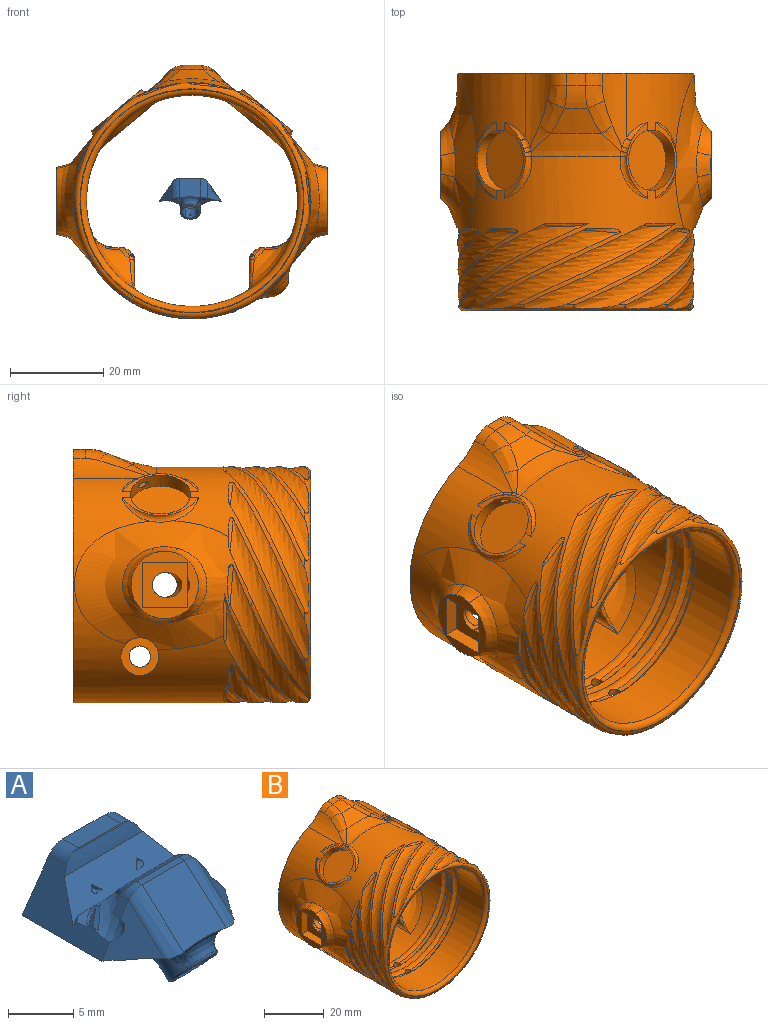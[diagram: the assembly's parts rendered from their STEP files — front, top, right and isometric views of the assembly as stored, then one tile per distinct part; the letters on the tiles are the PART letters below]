
ASSEMBLY  parts=2 mates=1
PART A: 99 faces, bbox 25.1x15.8x9.1 mm
  f0: cylinder r=22.62mm len=9.01mm, axis (0,1,0), area 27.3mm2, adj f1,f94,f95,f96,f97,f98
  f1: bspline ~7.37x6.18mm, area 15mm2, adj f0,f2,f93,f98
  f2: bspline ~5.24x2.07mm, area 1.4mm2, adj f1,f3,f90,f91,f92,f98
  f3: plane 0.6x0.26mm, normal (0,-0.74,-0.67), area 0.1mm2, adj f2,f4,f89
  f4: torus R=3.45mm, axis (0,0.74,0.67), area 0.5mm2, adj f3,f5,f85,f92
  f5: sphere r=1.27mm, area 1.7mm2, adj f4,f6,f89
  f6: bspline ~3.09x2.93mm, area 4.8mm2, adj f5,f7,f84,f85
  f7: cylinder r=22.62mm len=2.43mm, axis (0,1,0), area 1.8mm2, adj f6,f8,f89,f90,f98
  f8: extruded ~4.89x4.5mm, area 9.2mm2, adj f7,f9,f83,f84,f98
  f9: cylinder r=1.78mm len=1.46mm, axis (0,1,0), area 1.3mm2, adj f8,f10,f81,f82
  f10: plane 4.57x0.58mm, normal (0,0,1), area 2.6mm2, adj f9,f11,f80,f83
  f11: cylinder r=1.78mm len=1.46mm, axis (0,1,0), area 1.3mm2, adj f10,f12,f78,f79
  f12: extruded ~4.89x4.5mm, area 9.2mm2, adj f11,f13,f76,f77,f83
  f13: cylinder r=22.62mm len=2.43mm, axis (0,1,0), area 1.8mm2, adj f12,f14,f74,f75,f77
  f14: bspline ~3.01x1.22mm, area 1.1mm2, adj f13,f15,f74,f77
  f15: bspline ~5.24x2.07mm, area 1.4mm2, adj f14,f16,f19,f72,f73,f77
  f16: plane 0.6x0.26mm, normal (0,-0.74,-0.67), area 0.1mm2, adj f15,f17,f74
  f17: torus R=3.45mm, axis (0,0.74,0.67), area 0.5mm2, adj f16,f18,f19,f85
  f18: sphere r=1.27mm, area 1.9mm2, adj f17,f74,f75
  f19: bspline ~2.56x1.98mm, area 2.3mm2, adj f15,f17,f20,f85
  f20: bspline ~0.88x0.63mm, area 0.1mm2, adj f19,f21,f71,f72
  f21: plane 5.28x2.07mm, normal (-1,0,0), area 2.4mm2, adj f20,f22,f70,f71,f72,f95
  f22: cylinder r=1.14mm len=3.88mm, axis (0,1,0), area 5.6mm2, adj f21,f23,f70,f95
  f23: cylinder r=22.62mm len=9.01mm, axis (0,1,0), area 27.3mm2, adj f22,f24,f73,f77,f95,f96
  f24: plane 8.68x4.33mm, normal (-0.82,0,0.57), area 24.6mm2, adj f23,f25,f54,f61,f62,f67,f68,f69
  f25: bspline ~12.73x12.04mm, area 13.1mm2, adj f24,f26,f28,f39,f49,f51,f52,f53
  f26: bspline ~2.41x2.24mm, area 1.1mm2, adj f25,f27,f69
  f27: plane 2.04x1.79mm, normal (-0.49,0.45,0.75), area 1mm2, adj f26,f69
  f28: plane 10.42x1.4mm, normal (0,0.74,0.67), area 7.1mm2, adj f25,f29,f30,f31,f34,f39,f62,f67
  f29: plane 0.84x0.62mm, normal (0.49,0.45,0.75), area 0.2mm2, adj f28,f30,f62,f97
  f30: cone r=1.65mm half-angle=45deg, axis (0.49,0.45,0.75), area 1.3mm2, adj f28,f29,f31,f97
  f31: cylinder r=1.65mm len=2.41mm, axis (0.49,0.45,0.75), area 0.8mm2, adj f28,f30,f32,f33,f34,f97
  f32: plane 2.04x1.79mm, normal (0.49,0.45,0.75), area 1mm2, adj f31,f33
  f33: bspline ~2.41x2.24mm, area 1.1mm2, adj f31,f32,f34
  f34: bspline ~12.73x12.04mm, area 13.1mm2, adj f28,f31,f33,f35,f37,f38,f39,f49
  f35: cone r=1.65mm half-angle=45deg, axis (0.49,0.45,0.75), area 1.2mm2, adj f34,f36,f38,f49,f82
  f36: plane 0.64x0.6mm, normal (0.49,0.45,0.75), area 0mm2, adj f35,f49,f81,f82
  f37: bspline ~1.57x1.5mm, area 0mm2, adj f34,f38
  f38: cylinder r=1.65mm len=2.12mm, axis (0.49,0.45,0.75), area 1.1mm2, adj f34,f35,f37,f82
  f39: cylinder r=1.68mm len=8.2mm, axis (0,-0.74,-0.67), area 62.2mm2, adj f25,f28,f34,f40,f46,f49
  f40: plane 3.86x2.87mm, normal (0,-0.74,-0.67), area 2.9mm2, adj f39,f41,f42,f44,f45,f46
  f41: bspline ~0.65x0.63mm, area 0.1mm2, adj f40,f42,f45,f76
  f42: bspline ~2.91x0.73mm, area 1mm2, adj f40,f41,f43,f44
  f43: bspline ~4.87x2.01mm, area 6mm2, adj f42,f76,f83,f84
  f44: bspline ~0.68x0.65mm, area 0.1mm2, adj f40,f42,f45,f84
  f45: torus R=1.93mm, axis (0,-0.74,-0.67), area 3.9mm2, adj f40,f41,f44,f85
  f46: extruded ~4.61x4.6mm, area 22.2mm2, adj f39,f40,f47,f48
  f47: plane 0.47x0.42mm, normal (0,-0.65,0.76), area 0.2mm2, adj f46,f48
  f48: plane 0.55x0.13mm, normal (0,0.37,-0.93), area 0mm2, adj f46,f47
  f49: plane 6.3x1.74mm, normal (0,0.74,0.67), area 7.8mm2, adj f25,f34,f35,f36,f39,f50,f51,f79
  f50: plane 0.64x0.6mm, normal (-0.49,0.45,0.75), area 0mm2, adj f49,f51,f78,f79
  f51: cone r=2.16mm half-angle=45deg, axis (-0.49,0.45,0.75), area 1.2mm2, adj f25,f49,f50,f53,f78
  f52: bspline ~1.57x1.5mm, area 0mm2, adj f25,f53
  f53: cylinder r=1.65mm len=2.12mm, axis (-0.49,0.45,0.75), area 1.1mm2, adj f25,f51,f52,f78
  f54: cylinder r=1.78mm len=1.89mm, axis (0,1,0), area 2.9mm2, adj f24,f55,f60,f61,f96
  f55: plane 4.57x1.68mm, normal (0,0,1), area 7.7mm2, adj f54,f56,f59,f96
  f56: cylinder r=1.78mm len=1.89mm, axis (0,1,0), area 2.9mm2, adj f55,f57,f61,f96,f97
  f57: bspline ~2.18x1.54mm, area 0mm2, adj f56,f58,f59
  f58: plane 5.9x0.15mm, normal (0,-0.09,-1), area 0.5mm2, adj f57,f59,f60,f61
  f59: plane 4.57x0.11mm, normal (0,-0.91,0.41), area 0.6mm2, adj f55,f57,f58,f60
  f60: bspline ~0.64x0.22mm, area 0mm2, adj f54,f58,f59
  f61: extruded ~8.51x1.37mm, area 10.7mm2, adj f24,f54,f56,f58,f62,f97
  f62: plane 11.86x2.65mm, normal (0,-0.67,0.74), area 30.4mm2, adj f24,f28,f29,f61,f63,f64,f65,f66
  f63: plane 0.8x0.76mm, normal (-0.7,-0.71,-0.05), area 0.2mm2, adj f62,f64
  f64: bspline ~1.01x0.98mm, area 0.4mm2, adj f62,f63
  f65: plane 0.8x0.76mm, normal (0.7,-0.71,-0.05), area 0.2mm2, adj f62,f66
  f66: bspline ~1.01x0.98mm, area 0.4mm2, adj f62,f65
  f67: plane 0.84x0.62mm, normal (-0.49,0.45,0.75), area 0.2mm2, adj f24,f28,f62,f68
  f68: cone r=2.16mm half-angle=45deg, axis (-0.49,0.45,0.75), area 1.3mm2, adj f24,f28,f67,f69
  f69: cylinder r=1.65mm len=2.41mm, axis (-0.49,0.45,0.75), area 0.8mm2, adj f24,f25,f26,f27,f28,f68
  f70: bspline ~5.41x3.02mm, area 6.3mm2, adj f21,f22,f72,f73
  f71: cylinder r=1.14mm len=2.77mm, axis (0,0.74,0.67), area 1.7mm2, adj f20,f21,f85,f95
  f72: bspline ~0.93x0.84mm, area 0.1mm2, adj f15,f20,f21,f70
  f73: bspline ~7.32x6.17mm, area 15mm2, adj f15,f23,f70,f77
  f74: bspline ~1.04x0.84mm, area 0.7mm2, adj f13,f14,f16,f18
  f75: bspline ~3.21x3.17mm, area 4.8mm2, adj f13,f18,f76,f85
  f76: bspline ~2.38x2.3mm, area 0.8mm2, adj f12,f41,f43,f75,f85
  f77: plane 4.35x4.03mm, normal (-0.73,-0.46,0.51), area 10.2mm2, adj f12,f13,f14,f15,f23,f24,f25,f73
  f78: plane 1.34x1.03mm, normal (-0.82,0,0.57), area 1.3mm2, adj f11,f25,f50,f51,f53,f77
  f79: bspline ~1.46x0.96mm, area 1mm2, adj f11,f49,f50,f80
  f80: plane 4.57x0.57mm, normal (0,0.41,0.91), area 2.8mm2, adj f10,f49,f79,f81
  f81: bspline ~1.46x0.96mm, area 1mm2, adj f9,f36,f49,f80
  f82: plane 1.34x1.03mm, normal (0.82,0,0.57), area 1.3mm2, adj f9,f34,f35,f36,f38,f98
  f83: plane 4.71x4.64mm, normal (0,-0.67,0.74), area 27.2mm2, adj f8,f10,f12,f43
  f84: bspline ~2.21x2.14mm, area 0.8mm2, adj f6,f8,f43,f44,f85
  f85: cylinder r=2.18mm len=4.83mm, axis (0,0.74,0.67), area 15.5mm2, adj f4,f6,f17,f19,f45,f71,f75,f76
  f86: cylinder r=1.14mm len=2.77mm, axis (0,0.74,0.67), area 1.7mm2, adj f85,f87,f88,f95
  f87: plane 5.28x2.07mm, normal (1,0,0), area 2.4mm2, adj f86,f88,f91,f93,f94,f95
  f88: bspline ~0.93x0.6mm, area 0.1mm2, adj f86,f87,f91,f92
  f89: bspline ~1.04x0.84mm, area 0.7mm2, adj f3,f5,f7,f90
  f90: bspline ~3.01x1.22mm, area 1.1mm2, adj f2,f7,f89,f98
  f91: bspline ~0.96x0.88mm, area 0.1mm2, adj f2,f87,f88,f93
  f92: bspline ~2.56x1.98mm, area 2.3mm2, adj f2,f4,f85,f88
  f93: bspline ~5.41x3.02mm, area 6.3mm2, adj f1,f87,f91,f94
  f94: cylinder r=1.14mm len=3.88mm, axis (0,1,0), area 5.6mm2, adj f0,f87,f93,f95
  f95: plane 10.79x5.27mm, normal (0,0.37,-0.93), area 27mm2, adj f0,f21,f22,f23,f71,f85,f86,f87
  f96: plane 13.37x4.96mm, normal (0,1,0), area 39.8mm2, adj f0,f23,f24,f54,f55,f56,f97
  f97: plane 8.68x4.33mm, normal (0.82,0,0.57), area 24.6mm2, adj f0,f29,f30,f31,f34,f56,f61,f62
  f98: plane 4.35x4.03mm, normal (0.73,-0.46,0.51), area 10.2mm2, adj f0,f1,f2,f7,f8,f34,f82,f90
PART B: 277 faces, bbox 65.1x60.6x65.1 mm
  f0: cylinder r=7.23mm len=4mm, axis (-1,0,0), area 0mm2, adj f1,f276
  f1: plane 14.98x14.98mm, normal (-1,0,0), area 70mm2, adj f0,f2,f269,f270,f271,f272,f273,f274
  f2: cylinder r=7.23mm len=4mm, axis (-1,0,0), area 0mm2, adj f1,f3
  f3: bspline ~8.56x3.63mm, area 14.9mm2, adj f2,f4,f269,f270
  f4: bspline ~38.72x27.55mm, area 617.9mm2, adj f3,f5,f258,f259,f260,f261,f262,f263
  f5: cylinder r=4.06mm len=11.07mm, axis (-1,0,0), area 179.5mm2, adj f4,f6,f243,f244,f245,f246,f247,f248
  f6: bspline ~3.39x1.85mm, area 1.2mm2, adj f5,f7,f243,f257
  f7: cylinder r=1.4mm len=10.89mm, axis (0,1,0), area 9.7mm2, adj f6,f8,f33,f241,f242
  f8: plane 4.01x3.6mm, normal (1,0,0), area 4.9mm2, adj f7,f9,f243
  f9: bspline ~6.62x4.96mm, area 8.1mm2, adj f8,f10,f241,f242,f244
  f10: torus R=4.32mm, axis (1,0,0), area 1.1mm2, adj f9,f11,f32,f245
  f11: cylinder r=5.33mm len=8.95mm, axis (-1,0,0), area 9mm2, adj f10,f12,f19,f26,f31,f241
  f12: bspline ~6.6x5.33mm, area 15.1mm2, adj f11,f13,f31,f241
  f13: cylinder r=6.1mm len=12.19mm, axis (1,0,0), area 17.8mm2, adj f12,f14,f33
  f14: plane 18.15x18.15mm, normal (1,0,0), area 87.2mm2, adj f13,f15,f18
  f15: cylinder r=2.67mm len=5.33mm, axis (1,0,0), area 25.9mm2, adj f14,f16,f17,f18
  f16: plane 9.65x9.65mm, normal (-1,0,0), area 66mm2, adj f15,f17,f271,f272,f274,f275
  f17: cylinder r=2.63mm len=5.26mm, axis (-0.88,-0.48,0), area 14.3mm2, adj f15,f16
  f18: cylinder r=2.63mm len=5.26mm, axis (-0.88,-0.48,0), area 0mm2, adj f14,f15
  f19: bspline ~7.89x2.23mm, area 9mm2, adj f11,f20,f22,f23,f25,f32
  f20: bspline ~0.95x0.93mm, area 0.5mm2, adj f19,f21,f22,f251
  f21: cylinder r=1.27mm len=0.41mm, axis (0,-1,0), area 0mm2, adj f20,f25,f250
  f22: bspline ~1.34x1.3mm, area 0.4mm2, adj f19,f20,f26,f252
  f23: bspline ~1.21x1.2mm, area 0.5mm2, adj f19,f24,f32,f247
  f24: cylinder r=1.27mm len=0.41mm, axis (0,-1,0), area 0mm2, adj f23,f25,f248
  f25: plane 5.51x1.07mm, normal (0.71,0,0.71), area 1.6mm2, adj f19,f21,f24,f249
  f26: torus R=4.32mm, axis (1,0,0), area 1.1mm2, adj f11,f22,f27,f253
  f27: bspline ~5.73x3.96mm, area 8.3mm2, adj f26,f28,f30,f31,f254
  f28: bspline ~4.78x1.91mm, area 2.3mm2, adj f27,f29,f31
  f29: cylinder r=1.4mm len=10.89mm, axis (0,1,0), area 10.4mm2, adj f28,f30,f33,f256
  f30: plane 4x3.6mm, normal (1,0,0), area 4.9mm2, adj f27,f29,f255
  f31: bspline ~15.45x15.15mm, area 101.4mm2, adj f11,f12,f27,f28,f33
  f32: bspline ~1.38x1.27mm, area 0.3mm2, adj f10,f19,f23,f246
  f33: cylinder r=22.62mm len=45.24mm, axis (0,1,0), area 2155mm2, adj f7,f13,f29,f31,f34,f36,f38,f213
  f34: bspline ~21x13.67mm, area 169.3mm2, adj f33,f35
  f35: plane 16.09x12.82mm, normal (-0.64,0,-0.77), area 153.3mm2, adj f34
  f36: bspline ~21x13.67mm, area 169.3mm2, adj f33,f37
  f37: plane 16.29x13.03mm, normal (0.64,0,-0.77), area 153.3mm2, adj f36
  f38: cylinder r=1.4mm len=10.89mm, axis (0,1,0), area 9.7mm2, adj f33,f39,f211,f212,f217
  f39: plane 4x3.6mm, normal (-1,0,0), area 4.9mm2, adj f38,f40,f210
  f40: torus R=4.45mm, axis (1,0,0), area 2.4mm2, adj f39,f41,f209,f211
  f41: cylinder r=4.06mm len=8.13mm, axis (-1,0,0), area 132.2mm2, adj f40,f42,f58,f198,f199,f200,f201,f202
  f42: bspline ~5.16x1.41mm, area 4.7mm2, adj f41,f43,f198,f208
  f43: plane 5.51x1.07mm, normal (-0.71,0,0.71), area 1.6mm2, adj f42,f44,f56,f57
  f44: bspline ~7.89x2.23mm, area 9mm2, adj f43,f45,f46,f51,f54,f55
  f45: bspline ~0.95x0.93mm, area 0.5mm2, adj f44,f46,f57,f199
  f46: bspline ~1.06x1.03mm, area 0.4mm2, adj f44,f45,f47,f200
  f47: torus R=4.32mm, axis (1,0,0), area 1.1mm2, adj f46,f48,f51,f201
  f48: bspline ~6.62x4.96mm, area 8.1mm2, adj f47,f49,f50,f202,f215
  f49: bspline ~4.98x2.05mm, area 2.3mm2, adj f48,f214,f215
  f50: plane 4.01x3.6mm, normal (-1,0,0), area 4.9mm2, adj f48,f203,f214
  f51: cylinder r=5.33mm len=8.94mm, axis (-1,0,0), area 9mm2, adj f44,f47,f52,f53,f215,f217
  f52: bspline ~6.63x5.64mm, area 15.1mm2, adj f51,f215,f216,f217
  f53: torus R=4.32mm, axis (1,0,0), area 1.1mm2, adj f51,f54,f205,f210
  f54: bspline ~1.34x1.3mm, area 0.4mm2, adj f44,f53,f55,f206
  f55: bspline ~1.21x1.2mm, area 0.5mm2, adj f44,f54,f56,f207
  f56: cylinder r=1.27mm len=0.41mm, axis (0,-1,0), area 0mm2, adj f43,f55,f208
  f57: cylinder r=1.27mm len=0.41mm, axis (0,-1,0), area 0mm2, adj f43,f45,f198
  f58: plane 8.13x8.13mm, normal (-1,0,0), area 35.5mm2, adj f41,f59
  f59: cylinder r=2.29mm len=4.57mm, axis (-1,0,0), area 44.4mm2, adj f58,f60,f63,f64,f65,f66
  f60: bspline ~8.22x8.05mm, area 33.7mm2, adj f59,f61,f63,f66,f258
  f61: bspline ~6.51x3.43mm, area 10.6mm2, adj f60,f62,f64,f258
  f62: cylinder r=5.33mm len=2.68mm, axis (-1,0,0), area 0mm2, adj f61,f63
  f63: torus R=0.76mm, axis (1,0,0), area 34.6mm2, adj f59,f60,f62,f64
  f64: bspline ~8.05x7.79mm, area 33.4mm2, adj f59,f61,f63,f65,f66,f258
  f65: cylinder r=4.57mm len=0.21mm, axis (0,1,0), area 0mm2, adj f59,f64,f66
  f66: bspline ~38.66x27.57mm, area 651.6mm2, adj f59,f60,f64,f65,f67,f81,f82,f84
  f67: bspline ~15.67x7.05mm, area 56.5mm2, adj f66,f68,f81,f197
  f68: plane 14.98x14.98mm, normal (1,0,0), area 70mm2, adj f67,f69,f70,f71,f72,f78,f79,f80
  f69: cylinder r=7.23mm len=4mm, axis (1,0,0), area 0mm2, adj f68,f81
  f70: cylinder r=7.23mm len=4mm, axis (1,0,0), area 0mm2, adj f68,f197
  f71: cylinder r=2.63mm len=3mm, axis (0.88,-0.48,0), area 0mm2, adj f68,f80
  f72: plane 9.65x3.05mm, normal (0,0,1), area 29.4mm2, adj f68,f73,f78,f80
  f73: plane 9.65x9.65mm, normal (1,0,0), area 66mm2, adj f72,f74,f75,f78,f79,f80
  f74: cylinder r=2.63mm len=5.26mm, axis (0.88,-0.48,0), area 14.3mm2, adj f73,f75
  f75: cylinder r=2.67mm len=5.33mm, axis (1,0,0), area 25.9mm2, adj f73,f74,f76,f77
  f76: plane 18.15x18.15mm, normal (-1,0,0), area 87.2mm2, adj f75,f77,f216
  f77: cylinder r=2.63mm len=5.26mm, axis (0.88,-0.48,0), area 0mm2, adj f75,f76
  f78: plane 9.65x3.05mm, normal (0,-1,0), area 29.4mm2, adj f68,f72,f73,f79
  f79: plane 9.65x3.05mm, normal (0,0,-1), area 29.4mm2, adj f68,f73,f78,f80
  f80: plane 11.35x4.75mm, normal (0,1,0), area 27.4mm2, adj f68,f71,f72,f73,f79
  f81: bspline ~9.08x3.85mm, area 14.9mm2, adj f66,f67,f69,f196
  f82: bspline ~3.32x2.19mm, area 0.7mm2, adj f66,f83,f84
  f83: torus R=24.4mm, axis (0,-1,0), area 5.7mm2, adj f82,f84,f258
  f84: bspline ~45.41x20.32mm, area 167.7mm2, adj f66,f82,f83,f85,f114,f258
  f85: torus R=24.02mm, axis (0,1,0), area 205mm2, adj f84,f86,f88,f89,f100,f102,f104,f106
  f86: bspline ~45.84x20.32mm, area 164.1mm2, adj f85,f87,f260
  f87: torus R=24.4mm, axis (0,-1,0), area 6.5mm2, adj f86,f260
  f88: torus R=24.02mm, axis (0,1,0), area 0mm2, adj f85,f116,f117
  f89: plane 48.03x48.03mm, normal (0,-1,0), area 19.1mm2, adj f85,f90
  f90: torus R=23.89mm, axis (0,1,0), area 289.3mm2, adj f89,f91
  f91: cylinder r=22.62mm len=45.24mm, axis (0,1,0), area 1562.7mm2, adj f90,f92
  f92: torus R=22.11mm, axis (0,1,0), area 243.7mm2, adj f91,f93,f99
  f93: cylinder r=1.27mm len=2.54mm, axis (0,0,1), area 10.9mm2, adj f92,f94,f99,f104
  f94: torus R=22.11mm, axis (0,1,0), area 243.7mm2, adj f93,f95,f99
  f95: cylinder r=22.62mm len=45.24mm, axis (0,1,0), area 273.8mm2, adj f94,f96
  f96: torus R=22.11mm, axis (0,1,0), area 243.7mm2, adj f95,f97,f98
  f97: cylinder r=1.27mm len=2.54mm, axis (0,0,1), area 13.2mm2, adj f96,f98,f223,f258
  f98: cylinder r=23.79mm len=47.57mm, axis (0,1,0), area 174.3mm2, adj f96,f97,f223
  f99: cylinder r=23.79mm len=47.57mm, axis (0,1,0), area 174.3mm2, adj f92,f93,f94
  f100: bspline ~43.97x21.94mm, area 164.1mm2, adj f85,f101,f258
  f101: torus R=24.4mm, axis (0,-1,0), area 6.5mm2, adj f100,f258
  f102: bspline ~35.51x33.27mm, area 147.4mm2, adj f85,f103,f258
  f103: bspline ~9.96x3.03mm, area 0mm2, adj f102,f258
  f104: bspline ~42.71x24.3mm, area 166.1mm2, adj f85,f93,f105,f258
  f105: torus R=24.4mm, axis (0,-1,0), area 6.5mm2, adj f104,f258
  f106: bspline ~45.84x20.32mm, area 147.4mm2, adj f85,f107,f258
  f107: bspline ~8.25x7.24mm, area 0mm2, adj f106,f258
  f108: bspline ~43.97x21.94mm, area 147.4mm2, adj f85,f109,f260
  f109: bspline ~8.59x6.83mm, area 0mm2, adj f108,f260
  f110: bspline ~35.51x33.27mm, area 164.1mm2, adj f85,f111,f260
  f111: torus R=24.4mm, axis (0,-1,0), area 6.5mm2, adj f110,f260
  f112: bspline ~42.71x24.3mm, area 147.4mm2, adj f85,f113,f260
  f113: bspline ~9.82x3.52mm, area 0mm2, adj f112,f260
  f114: cylinder r=25.29mm len=20.1mm, axis (0,1,0), area 23.9mm2, adj f66,f84,f85,f116
  f115: bspline ~12.27x1.61mm, area 0mm2, adj f66,f116
  f116: bspline ~38.75x29.76mm, area 155.4mm2, adj f66,f85,f88,f114,f115,f117
  f117: cylinder r=25.29mm len=25.96mm, axis (0,1,0), area 30.1mm2, adj f66,f85,f88,f116,f118
  f118: bspline ~40.31x27.89mm, area 154.5mm2, adj f66,f85,f117,f119,f260
  f119: bspline ~10.14x5.35mm, area 3.5mm2, adj f66,f118,f260
  f120: bspline ~16.5x7.09mm, area 20.2mm2, adj f66,f121,f122,f258,f260
  f121: cylinder r=6.99mm len=1.71mm, axis (0.64,0,0.77), area 0mm2, adj f120,f122
  f122: plane 16.87x5.02mm, normal (0.64,0,0.77), area 15.2mm2, adj f120,f121,f123,f258,f260
  f123: cylinder r=6.48mm len=12.95mm, axis (0.64,0,0.77), area 121.4mm2, adj f122,f124,f193,f194,f195,f258,f260
  f124: bspline ~9.24x8.08mm, area 55.1mm2, adj f123,f125,f127,f128,f192,f193,f226,f227
  f125: plane 0.91x0.6mm, normal (0.73,-0.46,0.51), area 0.3mm2, adj f124,f126,f127,f227
  f126: plane 0.91x0.89mm, normal (0.23,-0.65,0.72), area 0.3mm2, adj f125,f127,f226,f227
  f127: plane 0.87x0.79mm, normal (0.16,-0.99,0.04), area 0.2mm2, adj f124,f125,f126,f226
  f128: plane 2.07x1.92mm, normal (0.16,-0.99,0.04), area 0.7mm2, adj f124,f129,f191,f192,f226
  f129: extruded ~0.4x0.32mm, area 0mm2, adj f128,f130,f191,f192
  f130: cylinder r=2.03mm len=8.49mm, axis (0,1,0), area 14.4mm2, adj f129,f131,f174,f175,f176,f177,f178,f191
  f131: plane 4.57x1.49mm, normal (0,0,-1), area 6.8mm2, adj f130,f132,f174,f191
  f132: cylinder r=2.03mm len=8.49mm, axis (0,1,0), area 14.4mm2, adj f131,f133,f171,f172,f174,f176,f177,f178
  f133: extruded ~0.4x0.32mm, area 0mm2, adj f132,f134,f171,f191
  f134: plane 2.07x1.92mm, normal (-0.16,-0.99,0.04), area 0.7mm2, adj f133,f135,f171,f191,f221
  f135: bspline ~9.24x8.08mm, area 55.1mm2, adj f134,f136,f137,f168,f170,f171,f220,f221
  f136: extruded ~1.73x1.69mm, area 0mm2, adj f135,f137
  f137: cylinder r=6.48mm len=12.95mm, axis (-0.64,0,0.77), area 121.4mm2, adj f135,f136,f138,f139,f166,f258,f260
  f138: plane 12.95x9.92mm, normal (-0.64,0,0.77), area 131.8mm2, adj f137
  f139: plane 16.86x5.01mm, normal (-0.64,0,0.77), area 15.2mm2, adj f137,f140,f141,f162,f163,f164,f165,f258
  f140: bspline ~6.73x5.44mm, area 4.2mm2, adj f139,f141,f258
  f141: bspline ~3.06x2.72mm, area 2.8mm2, adj f139,f140,f142,f162
  f142: cylinder r=13.97mm len=15.7mm, axis (0,1,0), area 73.4mm2, adj f141,f143,f159,f160,f161,f178,f258
  f143: bspline ~9.16x7.24mm, area 10.7mm2, adj f142,f144,f159,f162
  f144: torus R=39.26mm, axis (0,1,0), area 81.5mm2, adj f143,f145,f157,f158,f163,f260
  f145: bspline ~3.01x1.74mm, area 1.5mm2, adj f144,f146,f155,f156,f194
  f146: bspline ~2.41x1.95mm, area 1.5mm2, adj f145,f147,f157,f194
  f147: bspline ~3.43x2.83mm, area 2.8mm2, adj f146,f148,f149,f194
  f148: bspline ~6.73x5.44mm, area 4.2mm2, adj f147,f194,f258
  f149: cylinder r=13.97mm len=15.7mm, axis (0,1,0), area 73.4mm2, adj f147,f150,f153,f154,f157,f178,f258
  f150: cylinder r=5.08mm len=3.7mm, axis (0,-1,0), area 11mm2, adj f149,f151,f153,f178
  f151: cylinder r=29.1mm len=3.89mm, axis (0,1,0), area 9.9mm2, adj f150,f152,f161,f178
  f152: torus R=15.13mm, axis (0,-1,0), area 22.5mm2, adj f151,f153,f158,f160
  f153: bspline ~9.36x4.49mm, area 18.1mm2, adj f149,f150,f152,f154
  f154: bspline ~9.04x6.04mm, area 23.3mm2, adj f149,f153,f157,f158
  f155: bspline ~10.87x7.86mm, area 11.3mm2, adj f145,f156,f194,f260
  f156: cylinder r=6.99mm len=1.69mm, axis (0.64,0,0.77), area 0mm2, adj f145,f155,f194
  f157: bspline ~9.16x7.24mm, area 10.7mm2, adj f144,f146,f149,f154
  f158: cone r=29.1mm half-angle=20.6deg, axis (0,1,0), area 46.8mm2, adj f144,f152,f154,f159
  f159: bspline ~10.91x6.7mm, area 23.4mm2, adj f142,f143,f158,f160
  f160: bspline ~9.36x4.49mm, area 18.1mm2, adj f142,f152,f159,f161
  f161: cylinder r=5.08mm len=3.7mm, axis (0,1,0), area 11mm2, adj f142,f151,f160,f178
  f162: bspline ~3.13x2.12mm, area 1.5mm2, adj f139,f141,f143,f163
  f163: bspline ~4.25x2.19mm, area 1.5mm2, adj f139,f144,f162,f164,f165
  f164: cylinder r=6.99mm len=1.69mm, axis (-0.64,0,0.77), area 0mm2, adj f139,f163,f165
  f165: bspline ~10.87x7.86mm, area 11.3mm2, adj f139,f163,f164,f260
  f166: plane 16.87x5.02mm, normal (-0.64,0,0.77), area 15.2mm2, adj f137,f167,f258,f259,f260
  f167: cylinder r=6.99mm len=1.71mm, axis (-0.64,0,0.77), area 0mm2, adj f166,f259
  f168: plane 0.91x0.6mm, normal (-0.73,-0.46,0.51), area 0.3mm2, adj f135,f169,f170,f220
  f169: plane 0.91x0.89mm, normal (-0.23,-0.65,0.72), area 0.3mm2, adj f168,f170,f220,f221
  f170: plane 0.87x0.79mm, normal (-0.16,-0.99,0.04), area 0.2mm2, adj f135,f168,f169,f221
  f171: plane 1.79x1.36mm, normal (-0.73,-0.46,0.51), area 0.2mm2, adj f132,f133,f134,f135,f220
  f172: plane 2.76x0.85mm, normal (1,0,0), area 1.5mm2, adj f132,f173,f174,f176
  f173: cylinder r=1.27mm len=5.84mm, axis (-1,0,0), area 11.7mm2, adj f172,f174,f175,f176
  f174: plane 5.9x0.63mm, normal (0,0.67,-0.74), area 3.7mm2, adj f130,f131,f132,f172,f173,f175
  f175: plane 2.76x0.85mm, normal (-1,0,0), area 1.5mm2, adj f130,f173,f174,f176
  f176: plane 5.89x0.48mm, normal (0,-0.74,-0.67), area 2.6mm2, adj f130,f132,f172,f173,f175,f177
  f177: plane 4.57x4.45mm, normal (0,0,-1), area 20.3mm2, adj f130,f132,f176,f178
  f178: plane 54.36x50.57mm, normal (0,1,0), area 281.5mm2, adj f130,f132,f142,f149,f150,f151,f161,f177
  f179: bspline ~3.15x2.37mm, area 1.3mm2, adj f178,f180,f238,f239
  f180: bspline ~13.02x11.85mm, area 11.1mm2, adj f178,f179,f181,f185
  f181: bspline ~35.77x17.91mm, area 139.4mm2, adj f180,f182,f184,f218,f239
  f182: bspline ~3.64x1.93mm, area 2.1mm2, adj f181,f183,f218,f241
  f183: bspline ~4.63x2.79mm, area 4.6mm2, adj f182,f184,f240,f241
  f184: bspline ~4.26x3.17mm, area 7mm2, adj f181,f183,f240
  f185: bspline ~2.23x0.82mm, area 0.6mm2, adj f178,f180,f218,f219
  f186: bspline ~3.31x2.12mm, area 1.3mm2, adj f178,f187,f228,f229
  f187: bspline ~13.94x10.81mm, area 11.1mm2, adj f178,f186,f188,f190
  f188: bspline ~36.76x15.67mm, area 139.4mm2, adj f187,f189,f229,f233
  f189: bspline ~4.22x3.05mm, area 6.5mm2, adj f188,f230,f231,f232
  f190: bspline ~2.21x0.95mm, area 0.6mm2, adj f178,f187,f233,f234
  f191: plane 8.27x0.7mm, normal (0,-0.74,-0.67), area 0.7mm2, adj f128,f129,f130,f131,f132,f133,f134,f221
  f192: plane 1.79x1.36mm, normal (0.73,-0.46,0.51), area 0.2mm2, adj f124,f128,f129,f130,f227
  f193: extruded ~1.73x1.69mm, area 0mm2, adj f123,f124
  f194: plane 16.86x5.01mm, normal (0.64,0,0.77), area 15.2mm2, adj f123,f145,f146,f147,f148,f155,f156,f258
  f195: plane 12.95x9.92mm, normal (0.64,0,0.77), area 131.8mm2, adj f123
  f196: bspline ~15.67x7.06mm, area 56.5mm2, adj f66,f68,f81,f197
  f197: bspline ~7.96x3.72mm, area 14.9mm2, adj f66,f67,f70,f196
  f198: bspline ~1.24x1.05mm, area 0.4mm2, adj f41,f42,f57,f199
  f199: bspline ~0.71x0.7mm, area 0.3mm2, adj f41,f45,f198,f200
  f200: bspline ~0.52x0.52mm, area 0.1mm2, adj f41,f46,f199,f201
  f201: torus R=4.45mm, axis (-1,0,0), area 0.5mm2, adj f41,f47,f200,f202
  f202: bspline ~2.28x1.34mm, area 0.9mm2, adj f41,f48,f201,f203
  f203: torus R=4.45mm, axis (1,0,0), area 2.4mm2, adj f41,f50,f202,f204
  f204: bspline ~3.39x1.85mm, area 1.2mm2, adj f41,f203,f213,f214
  f205: torus R=4.45mm, axis (-1,0,0), area 0.5mm2, adj f41,f53,f206,f209
  f206: bspline ~0.48x0.48mm, area 0.1mm2, adj f41,f54,f205,f207
  f207: bspline ~0.91x0.89mm, area 0.3mm2, adj f41,f55,f206,f208
  f208: bspline ~1.24x1.05mm, area 0.4mm2, adj f41,f42,f56,f207
  f209: bspline ~2.28x1.34mm, area 0.9mm2, adj f40,f41,f205,f210
  f210: bspline ~5.73x3.96mm, area 8.3mm2, adj f39,f53,f209,f212,f217
  f211: bspline ~3.39x1.85mm, area 1.2mm2, adj f38,f40,f41,f213
  f212: bspline ~5.05x2.13mm, area 2.3mm2, adj f38,f210,f217
  f213: bspline ~2.74x0.55mm, area 0.4mm2, adj f33,f41,f204,f211
  f214: cylinder r=1.4mm len=10.89mm, axis (0,1,0), area 10.4mm2, adj f33,f49,f50,f204
  f215: bspline ~14.54x13.85mm, area 141.1mm2, adj f33,f48,f49,f51,f52
  f216: cylinder r=6.1mm len=12.19mm, axis (1,0,0), area 17.8mm2, adj f33,f52,f76
  f217: bspline ~13.56x13.38mm, area 101.2mm2, adj f33,f38,f51,f52,f210,f212
  f218: bspline ~29.94x15.73mm, area 33.1mm2, adj f33,f181,f182,f185
  f219: torus R=23mm, axis (0,-1,0), area 1.1mm2, adj f33,f178,f185,f220
  f220: plane 8.74x4.66mm, normal (0.82,0,-0.57), area 41.9mm2, adj f33,f132,f135,f168,f169,f171,f178,f219
  f221: plane 5.15x5.07mm, normal (0.73,0.46,-0.51), area 13.6mm2, adj f33,f134,f135,f169,f170,f191,f222
  f222: extruded ~5.25x4.83mm, area 11.6mm2, adj f33,f191,f221,f224
  f223: torus R=22.11mm, axis (0,1,0), area 243.7mm2, adj f33,f97,f98
  f224: plane 4.88x4.64mm, normal (0,0.67,-0.74), area 29.2mm2, adj f33,f191,f222,f225
  f225: extruded ~5.25x4.83mm, area 11.6mm2, adj f33,f191,f224,f226
  f226: plane 5.15x5.07mm, normal (-0.73,0.46,-0.51), area 13.6mm2, adj f33,f124,f126,f127,f128,f191,f225
  f227: plane 8.74x4.66mm, normal (-0.82,0,-0.57), area 41.9mm2, adj f33,f124,f125,f126,f130,f178,f192,f228
  f228: torus R=23mm, axis (0,-1,0), area 20mm2, adj f33,f178,f186,f227
  f229: bspline ~20.63x6.24mm, area 17.5mm2, adj f33,f186,f188,f230
  f230: bspline ~2.9x1.48mm, area 2.5mm2, adj f33,f189,f229,f231
  f231: bspline ~1.21x0.88mm, area 0.6mm2, adj f33,f189,f230,f232
  f232: bspline ~2.4x1.86mm, area 2.4mm2, adj f33,f189,f231,f233
  f233: bspline ~33.04x14.22mm, area 35.2mm2, adj f33,f188,f190,f232
  f234: torus R=23mm, axis (0,-1,0), area 2mm2, adj f33,f178,f190,f235
  f235: plane 7.66x3.82mm, normal (-0.38,0.92,0), area 22.3mm2, adj f33,f178,f234,f236,f258
  f236: plane 2.69x1.02mm, normal (0,1,0), area 2.7mm2, adj f33,f235,f237,f258
  f237: plane 3.18x2.68mm, normal (1,0,0), area 8.4mm2, adj f33,f178,f236,f238,f258
  f238: torus R=23mm, axis (0,-1,0), area 24.8mm2, adj f33,f178,f179,f237
  f239: bspline ~19.63x5.92mm, area 17.5mm2, adj f33,f179,f181,f240
  f240: bspline ~1.37x1.08mm, area 0.8mm2, adj f33,f183,f184,f239
  f241: bspline ~14.54x13.85mm, area 129.3mm2, adj f7,f9,f11,f12,f33,f182,f183,f242
  f242: bspline ~5.05x2.13mm, area 2.3mm2, adj f7,f9,f241
  f243: torus R=4.45mm, axis (1,0,0), area 2.4mm2, adj f5,f6,f8,f244
  f244: bspline ~2.56x1.35mm, area 0.9mm2, adj f5,f9,f243,f245
  f245: torus R=4.45mm, axis (-1,0,0), area 0.5mm2, adj f5,f10,f244,f246
  f246: bspline ~0.53x0.53mm, area 0.1mm2, adj f5,f32,f245,f247
  f247: bspline ~0.91x0.89mm, area 0.3mm2, adj f5,f23,f246,f248
  f248: bspline ~1.24x1.05mm, area 0.4mm2, adj f5,f24,f247,f249
  f249: bspline ~5.16x1.41mm, area 4.7mm2, adj f5,f25,f248,f250
  f250: bspline ~1.24x1.05mm, area 0.4mm2, adj f5,f21,f249,f251
  f251: bspline ~0.71x0.7mm, area 0.3mm2, adj f5,f20,f250,f252
  f252: bspline ~0.54x0.53mm, area 0.1mm2, adj f5,f22,f251,f253
  f253: torus R=4.45mm, axis (-1,0,0), area 0.5mm2, adj f5,f26,f252,f254
  f254: bspline ~2.56x1.35mm, area 0.9mm2, adj f5,f27,f253,f255
  f255: torus R=4.45mm, axis (1,0,0), area 2.4mm2, adj f5,f30,f254,f256
  f256: bspline ~3.39x1.85mm, area 1.2mm2, adj f5,f29,f255,f257
  f257: bspline ~2.74x0.55mm, area 0.4mm2, adj f5,f6,f33,f256
  f258: cylinder r=25.29mm len=50.57mm, axis (0,1,0), area 2231mm2, adj f4,f5,f60,f61,f64,f66,f83,f84
  f259: bspline ~16.5x7.09mm, area 20.1mm2, adj f4,f166,f167,f258,f260
  f260: cylinder r=25.29mm len=48.38mm, axis (0,1,0), area 743.2mm2, adj f4,f66,f85,f86,f87,f108,f109,f110
  f261: bspline ~9.25x5.51mm, area 3.3mm2, adj f4,f260,f262
  f262: bspline ~45.41x20.32mm, area 147.9mm2, adj f4,f85,f260,f261,f263
  f263: cylinder r=25.29mm len=20.1mm, axis (0,1,0), area 24mm2, adj f4,f85,f262,f265
  f264: bspline ~12.27x1.61mm, area 0mm2, adj f4,f265
  f265: bspline ~38.75x29.76mm, area 148.6mm2, adj f4,f85,f263,f264,f266
  f266: cylinder r=25.29mm len=25.96mm, axis (0,1,0), area 30mm2, adj f4,f85,f265,f267
  f267: bspline ~40.5x28.48mm, area 166.3mm2, adj f4,f85,f258,f266,f268
  f268: bspline ~13.51x5.16mm, area 7.2mm2, adj f4,f258,f267
  f269: bspline ~15.67x7.05mm, area 56.5mm2, adj f1,f3,f4,f276
  f270: bspline ~15.67x7.06mm, area 56.5mm2, adj f1,f3,f4,f276
  f271: plane 9.65x3.05mm, normal (0,-1,0), area 29.4mm2, adj f1,f16,f272,f275
  f272: plane 9.65x3.05mm, normal (0,0,1), area 29.4mm2, adj f1,f16,f271,f274
  f273: cylinder r=2.63mm len=3mm, axis (-0.88,-0.48,0), area 0mm2, adj f1,f274
  f274: plane 11.35x4.75mm, normal (0,1,0), area 27.4mm2, adj f1,f16,f272,f273,f275
  f275: plane 9.65x3.05mm, normal (0,0,-1), area 29.4mm2, adj f1,f16,f271,f274
  f276: bspline ~5.34x3.19mm, area 14.9mm2, adj f0,f4,f269,f270
PLACE A t=(-24.64,-18.56,-15.91)mm
PLACE B t=(-24.27,-18.56,5.86)mm
MATE planar A.f96 <-> B.f178  axis (0,1,0) through (-24.64,14.72,8.28)mm
